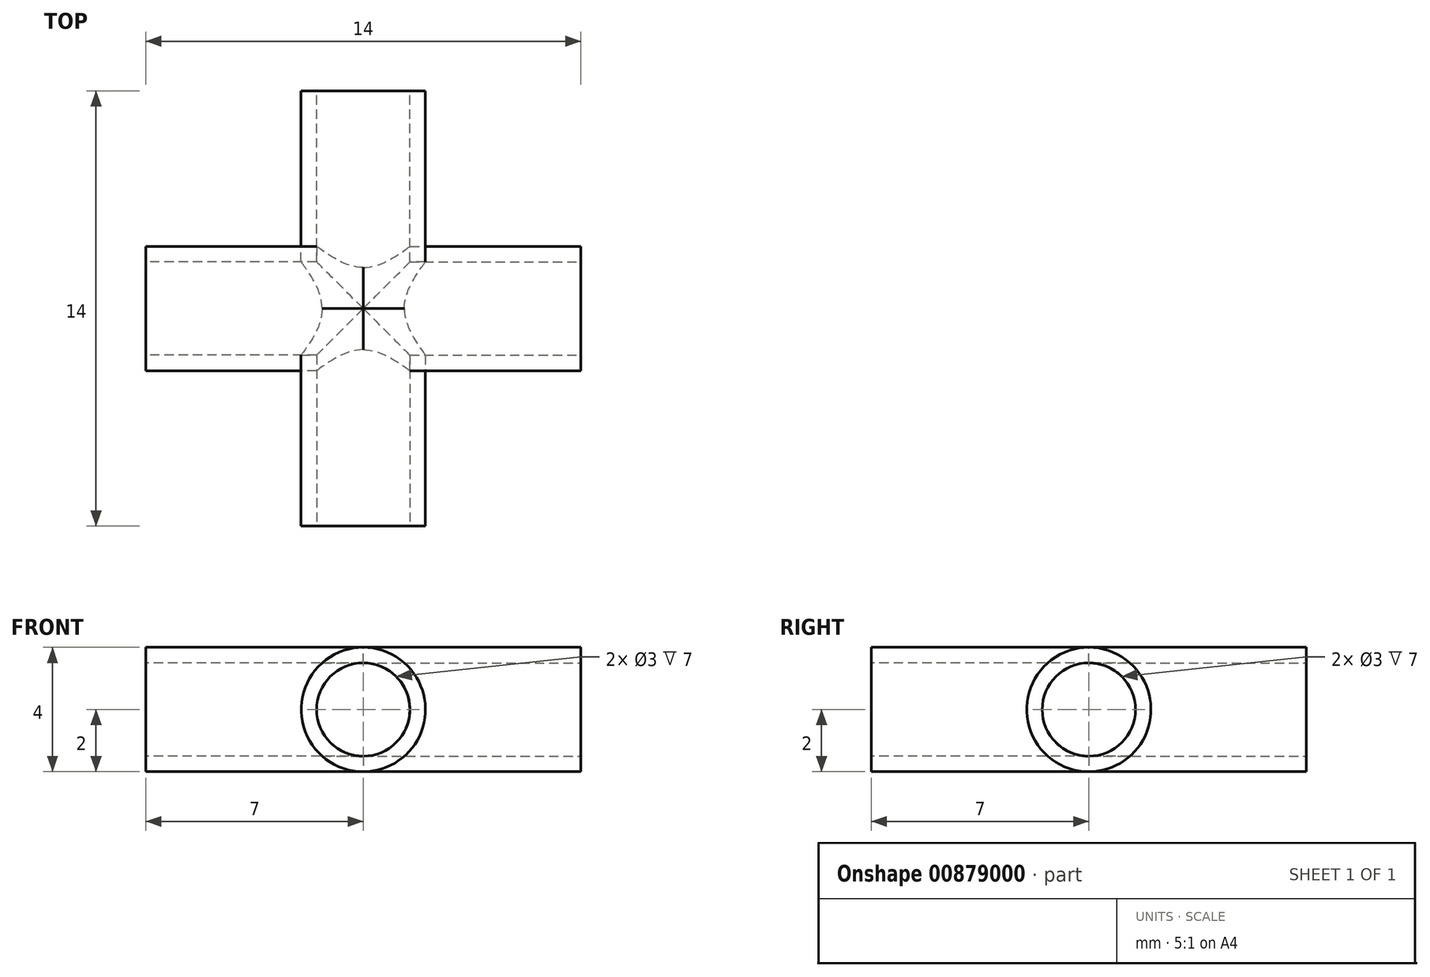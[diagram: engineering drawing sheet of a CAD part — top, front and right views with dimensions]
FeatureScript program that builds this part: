
annotation { "Feature Type Name" : "Feature", "Feature Type Description" : "" }
export const myFeature = defineFeature(function(context is Context, id is Id, definition is map)
    precondition{}
    {
        {
            var Q0;
            Q0=qCreatedBy(makeId("Front.planeOp"),FACE);
            var sketch = newSketch(context, id + "F0", { "sketchPlane" : qUnion([Q0])});
            skCircle(sketch, "E0", {"center": v(0, 0) * mm, "radius": 2 * mm});
            skCircle(sketch, "E1", {"center": v(0, 0) * mm, "radius": 1.5 * mm});
            skSolve(sketch);
        }
        {
            var Q0;
            Q0 = qSketchRegion(id + "F0", true);
            extrude(context, id + "F1", {"entities" : qUnion([Q0]), "endBound" : BoundingType.SYMMETRIC, "depth" : 10 * mm, "offsetDistance" : 25 * mm});
        }
        {
            var Q0;
            Q0=qCreatedBy(makeId("Right.planeOp"),FACE);
            var sketch = newSketch(context, id + "F2", { "sketchPlane" : qUnion([Q0])});
            skCircle(sketch, "E2", {"center": v(0, 0) * mm, "radius": 1.5 * mm});
            skLineSegment(sketch, "E3", {"start": v(0, 0) * mm, "end": v(0, 5.43) * mm});
            skLineSegment(sketch, "E4", {"start": v(0, 0) * mm, "end": v(0, -2.3) * mm});
            skLineSegment(sketch, "E5", {"start": v(0, 2.48) * mm, "end": v(-6.1, 2.48) * mm});
            skLineSegment(sketch, "E6", {"start": v(-6.1, 2.48) * mm, "end": v(-6.1, -2.66) * mm});
            skLineSegment(sketch, "E7", {"start": v(-6.1, -2.66) * mm, "end": v(0, -2.66) * mm});
            skLineSegment(sketch, "E8", {"start": v(0, -2.66) * mm, "end": v(0, -2.3) * mm});
            skSolve(sketch);
        }
        {
            var Q0;
            Q0 = qSketchRegion(id + "F2", true);
            extrude(context, id + "F3", {"entities" : qUnion([Q0]), "operationType" : NewBodyOperationType.REMOVE, "endBound" : BoundingType.SYMMETRIC, "depth" : 25 * mm, "offsetDistance" : 25 * mm});
        }
        {
            var Q0;
            Q0=makeQuery(id+"F3.boolean.opBoolean","SPLIT",BODY,{"disambiguationData":[OD(0.0)],"derivedFrom":makeQuery(id+"F1.opExtrude","SWEPT_BODY",BODY,{"disambiguationData":[OSD([sQuery(id+"F0.wireOp",EDGE,"E0"),sQuery(id+"F0.wireOp",EDGE,"E1")])]})});
            var Q1;
            Q1=sQuery(id+"F2.wireOp",EDGE,"E3");
            circularPattern(context, id + "F4", {"entities" : qUnion([Q0]), "axis" : qUnion([Q1]), "angle" : 360 * degree, "instanceCount" : 4, "equalSpace" : true});
        }
        {
            var Q0;
            Q0=makeQuery(id+"F4.opPattern","COPY",FACE,{"derivedFrom":makeQuery(id+"F1.opExtrude","CAP_FACE",FACE,{"disambiguationData":[OSD([sQuery(id+"F0.wireOp",EDGE,"E0"),sQuery(id+"F0.wireOp",EDGE,"E1")])],"isStart":true}),"instanceName":"1"});
            extrude(context, id + "F5", {"entities" : qUnion([Q0]), "operationType" : NewBodyOperationType.ADD, "depth" : 2 * mm, "offsetDistance" : 25 * mm});
        }
        {
            var Q0;
            Q0=makeQuery(id+"F4.opPattern","COPY",FACE,{"derivedFrom":makeQuery(id+"F1.opExtrude","CAP_FACE",FACE,{"disambiguationData":[OSD([sQuery(id+"F0.wireOp",EDGE,"E0"),sQuery(id+"F0.wireOp",EDGE,"E1")])],"isStart":true}),"instanceName":"2"});
            extrude(context, id + "F6", {"entities" : qUnion([Q0]), "operationType" : NewBodyOperationType.ADD, "depth" : 2 * mm, "offsetDistance" : 25 * mm});
        }
        {
            var Q0;
            Q0=makeQuery(id+"F4.opPattern","COPY",FACE,{"derivedFrom":makeQuery(id+"F1.opExtrude","CAP_FACE",FACE,{"disambiguationData":[OSD([sQuery(id+"F0.wireOp",EDGE,"E0"),sQuery(id+"F0.wireOp",EDGE,"E1")])],"isStart":true}),"instanceName":"3"});
            extrude(context, id + "F7", {"entities" : qUnion([Q0]), "operationType" : NewBodyOperationType.ADD, "depth" : 2 * mm, "offsetDistance" : 25 * mm});
        }
        {
            var Q0;
            Q0=makeQuery(id+"F1.opExtrude","CAP_FACE",FACE,{"disambiguationData":[OSD([sQuery(id+"F0.wireOp",EDGE,"E0"),sQuery(id+"F0.wireOp",EDGE,"E1")])],"isStart":true});
            extrude(context, id + "F8", {"entities" : qUnion([Q0]), "operationType" : NewBodyOperationType.ADD, "depth" : 2 * mm, "offsetDistance" : 25 * mm});
        }
    });
